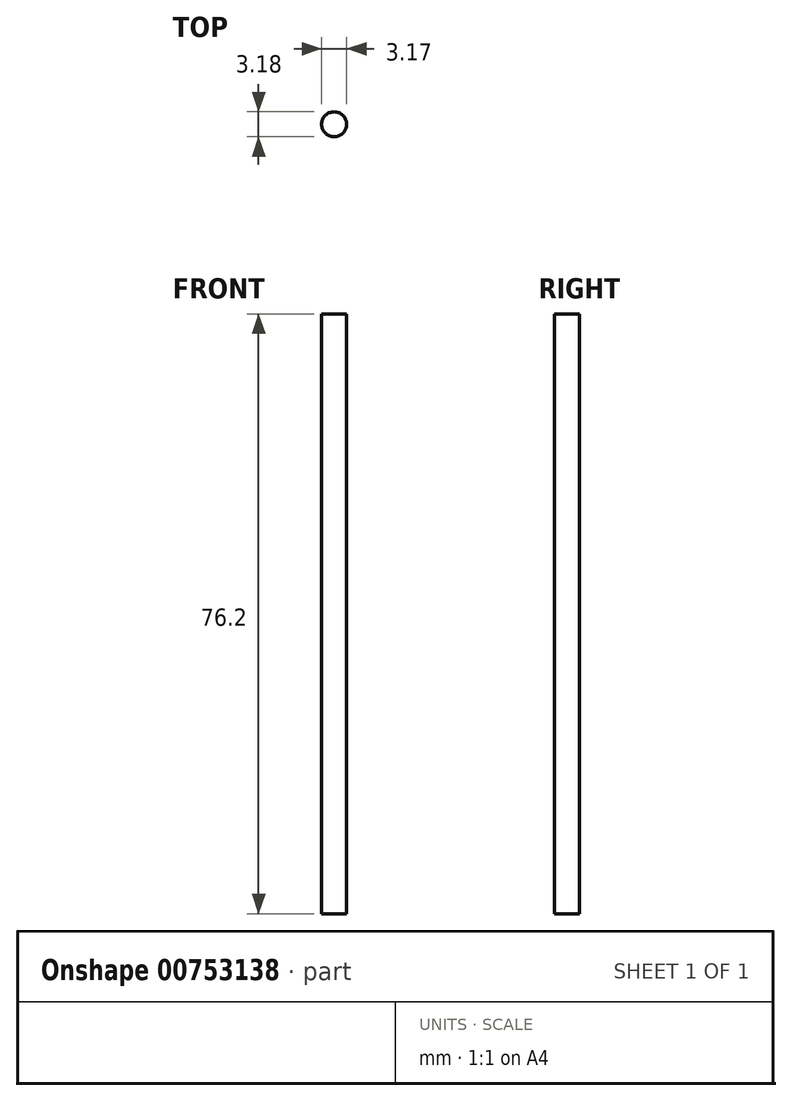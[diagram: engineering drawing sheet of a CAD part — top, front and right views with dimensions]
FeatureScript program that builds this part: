
annotation { "Feature Type Name" : "Feature", "Feature Type Description" : "" }
export const myFeature = defineFeature(function(context is Context, id is Id, definition is map)
    precondition{}
    {
        {
            var Q0;
            Q0=qCreatedBy(makeId("Top.planeOp"),FACE);
            var sketch = newSketch(context, id + "F0", { "sketchPlane" : qUnion([Q0])});
            skCircle(sketch, "E0", {"center": v(-87.13, -34.41) * mm, "radius": 1.59 * mm});
            skSolve(sketch);
        }
        {
            var Q0;
            Q0=makeQuery(id+"F0.imprint","IMPRINT",FACE,{"disambiguationData":[TD([[makeQuery(id+"F0.imprint","IMPRINT",EDGE,{"derivedFrom":sQuery(id+"F0.wireOp",EDGE,"E0")}),1.0]])]});
            extrude(context, id + "F1", {"entities" : qUnion([Q0]), "depth" : 76.2 * mm, "offsetDistance" : 25.4 * mm});
        }
    });
